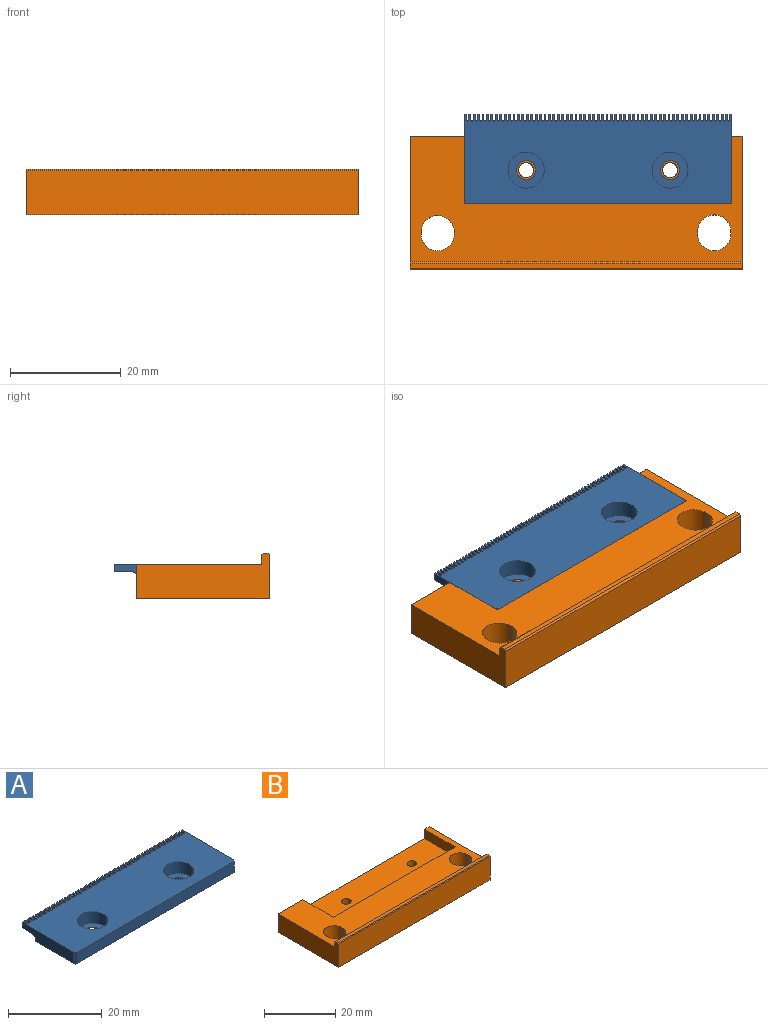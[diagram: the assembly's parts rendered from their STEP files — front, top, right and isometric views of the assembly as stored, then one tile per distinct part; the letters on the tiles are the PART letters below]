
ASSEMBLY  parts=2 mates=1
PART A: 260 faces, bbox 48.3x16.1x3.2 mm
  f0: plane 1.4x0.34mm, normal (0,1,0), area 0.5mm2, adj f67,f70,f71,f257
  f1: plane 1.4x0.34mm, normal (0,1,0), area 0.5mm2, adj f67,f73,f74,f257
  f2: plane 1.4x0.34mm, normal (0,1,0), area 0.5mm2, adj f67,f76,f77,f257
  f3: plane 1.4x0.34mm, normal (0,1,0), area 0.5mm2, adj f67,f79,f80,f257
  f4: plane 1.4x0.34mm, normal (0,1,0), area 0.5mm2, adj f67,f82,f83,f257
  f5: plane 1.4x0.34mm, normal (0,1,0), area 0.5mm2, adj f67,f85,f86,f257
  f6: plane 1.4x0.34mm, normal (0,1,0), area 0.5mm2, adj f67,f88,f89,f257
  f7: plane 1.4x0.34mm, normal (0,1,0), area 0.5mm2, adj f67,f91,f92,f257
  f8: plane 1.4x0.34mm, normal (0,1,0), area 0.5mm2, adj f67,f94,f95,f257
  f9: plane 1.4x0.34mm, normal (0,1,0), area 0.5mm2, adj f67,f97,f98,f257
  f10: plane 1.4x0.34mm, normal (0,1,0), area 0.5mm2, adj f67,f100,f101,f257
  f11: plane 1.4x0.34mm, normal (0,1,0), area 0.5mm2, adj f67,f103,f104,f257
  f12: plane 1.4x0.34mm, normal (0,1,0), area 0.5mm2, adj f67,f106,f107,f257
  f13: plane 1.4x0.34mm, normal (0,1,0), area 0.5mm2, adj f67,f109,f110,f257
  f14: plane 1.4x0.34mm, normal (0,1,0), area 0.5mm2, adj f67,f112,f113,f257
  f15: plane 1.4x0.34mm, normal (0,1,0), area 0.5mm2, adj f67,f115,f116,f257
  f16: plane 1.4x0.34mm, normal (0,1,0), area 0.5mm2, adj f67,f118,f119,f257
  f17: plane 1.4x0.34mm, normal (0,1,0), area 0.5mm2, adj f67,f121,f122,f257
  f18: plane 1.4x0.34mm, normal (0,1,0), area 0.5mm2, adj f67,f124,f125,f257
  f19: plane 1.4x0.34mm, normal (0,1,0), area 0.5mm2, adj f67,f127,f128,f257
  f20: plane 1.4x0.34mm, normal (0,1,0), area 0.5mm2, adj f67,f130,f131,f257
  f21: plane 1.4x0.34mm, normal (0,1,0), area 0.5mm2, adj f67,f133,f134,f257
  f22: plane 1.4x0.34mm, normal (0,1,0), area 0.5mm2, adj f67,f136,f137,f257
  f23: plane 1.4x0.34mm, normal (0,1,0), area 0.5mm2, adj f67,f139,f140,f257
  f24: plane 1.4x0.34mm, normal (0,1,0), area 0.5mm2, adj f67,f142,f143,f257
  f25: plane 1.4x0.34mm, normal (0,1,0), area 0.5mm2, adj f67,f145,f146,f257
  f26: plane 1.4x0.34mm, normal (0,1,0), area 0.5mm2, adj f67,f148,f149,f257
  f27: plane 1.4x0.34mm, normal (0,1,0), area 0.5mm2, adj f67,f151,f152,f257
  f28: plane 1.4x0.34mm, normal (0,1,0), area 0.5mm2, adj f67,f154,f155,f257
  f29: plane 1.4x0.34mm, normal (0,1,0), area 0.5mm2, adj f67,f157,f158,f257
  f30: plane 1.4x0.34mm, normal (0,1,0), area 0.5mm2, adj f67,f160,f161,f257
  f31: plane 1.4x0.34mm, normal (0,1,0), area 0.5mm2, adj f67,f163,f164,f257
  f32: plane 1.4x0.34mm, normal (0,1,0), area 0.5mm2, adj f67,f166,f167,f257
  f33: plane 1.4x0.34mm, normal (0,1,0), area 0.5mm2, adj f67,f169,f170,f257
  f34: plane 1.4x0.34mm, normal (0,1,0), area 0.5mm2, adj f67,f172,f173,f257
  f35: plane 1.4x0.34mm, normal (0,1,0), area 0.5mm2, adj f67,f175,f176,f257
  f36: plane 1.4x0.34mm, normal (0,1,0), area 0.5mm2, adj f67,f178,f179,f257
  f37: plane 1.4x0.34mm, normal (0,1,0), area 0.5mm2, adj f67,f181,f182,f257
  f38: plane 1.4x0.34mm, normal (0,1,0), area 0.5mm2, adj f67,f184,f185,f257
  f39: plane 1.4x0.34mm, normal (0,1,0), area 0.5mm2, adj f67,f187,f188,f257
  f40: plane 1.4x0.34mm, normal (0,1,0), area 0.5mm2, adj f67,f190,f191,f257
  f41: plane 1.4x0.34mm, normal (0,1,0), area 0.5mm2, adj f67,f193,f194,f257
  f42: plane 1.4x0.34mm, normal (0,1,0), area 0.5mm2, adj f67,f196,f197,f257
  f43: plane 1.4x0.34mm, normal (0,1,0), area 0.5mm2, adj f67,f199,f200,f257
  f44: plane 1.4x0.34mm, normal (0,1,0), area 0.5mm2, adj f67,f202,f203,f257
  f45: plane 1.4x0.34mm, normal (0,1,0), area 0.5mm2, adj f67,f205,f206,f257
  f46: plane 1.4x0.34mm, normal (0,1,0), area 0.5mm2, adj f67,f208,f209,f257
  f47: plane 1.4x0.34mm, normal (0,1,0), area 0.5mm2, adj f67,f211,f212,f257
  f48: plane 1.4x0.34mm, normal (0,1,0), area 0.5mm2, adj f67,f214,f215,f257
  f49: plane 1.4x0.34mm, normal (0,1,0), area 0.5mm2, adj f67,f217,f218,f257
  f50: plane 1.4x0.34mm, normal (0,1,0), area 0.5mm2, adj f67,f220,f221,f257
  f51: plane 1.4x0.34mm, normal (0,1,0), area 0.5mm2, adj f67,f223,f224,f257
  f52: plane 1.4x0.34mm, normal (0,1,0), area 0.5mm2, adj f67,f226,f227,f257
  f53: plane 1.4x0.34mm, normal (0,1,0), area 0.5mm2, adj f67,f229,f230,f257
  f54: plane 1.4x0.34mm, normal (0,1,0), area 0.5mm2, adj f67,f232,f233,f257
  f55: plane 1.4x0.34mm, normal (0,1,0), area 0.5mm2, adj f67,f235,f236,f257
  f56: plane 1.4x0.34mm, normal (0,1,0), area 0.5mm2, adj f67,f238,f239,f257
  f57: plane 1.4x0.34mm, normal (0,1,0), area 0.5mm2, adj f67,f241,f242,f257
  f58: plane 1.4x0.34mm, normal (0,1,0), area 0.5mm2, adj f67,f244,f245,f257
  f59: plane 15.6x2.85mm, normal (-1,0,0), area 38.7mm2, adj f62,f64,f67,f254,f257,f258,f259
  f60: plane 47.74x11.7mm, normal (0,0,-1), area 540.4mm2, adj f63,f64,f248,f251,f256,f259
  f61: plane 1.4x0.34mm, normal (0,1,0), area 0.5mm2, adj f66,f67,f68,f257
  f62: plane 1.4x0.34mm, normal (0,1,0), area 0.5mm2, adj f59,f67,f247,f257
  f63: plane 11.75x0.3mm, normal (0.71,0,-0.71), area 4.9mm2, adj f60,f66,f255,f256,f259
  f64: plane 11.75x0.3mm, normal (-0.71,0,-0.71), area 4.9mm2, adj f59,f60,f254,f256,f259
  f65: plane 47.34x2.85mm, normal (0,-1,0), area 134.9mm2, adj f67,f254,f255,f256
  f66: plane 15.6x2.85mm, normal (1,0,0), area 38.7mm2, adj f61,f63,f67,f255,f257,f258,f259
  f67: plane 48.34x16.1mm, normal (0,0,1), area 679.1mm2, adj f0,f1,f2,f3,f4,f5,f6,f7
  f68: plane 1.4x1mm, normal (-1,0,0), area 1.4mm2, adj f61,f67,f69,f257
  f69: cylinder r=0.23mm len=1.4mm, axis (0,0,-1), area 1mm2, adj f67,f68,f70,f257
  f70: plane 1.4x1mm, normal (1,0,0), area 1.4mm2, adj f0,f67,f69,f257
  f71: plane 1.4x1mm, normal (-1,0,0), area 1.4mm2, adj f0,f67,f72,f257
  f72: cylinder r=0.23mm len=1.4mm, axis (0,0,-1), area 1mm2, adj f67,f71,f73,f257
  f73: plane 1.4x1mm, normal (1,0,0), area 1.4mm2, adj f1,f67,f72,f257
  f74: plane 1.4x1mm, normal (-1,0,0), area 1.4mm2, adj f1,f67,f75,f257
  f75: cylinder r=0.23mm len=1.4mm, axis (0,0,-1), area 1mm2, adj f67,f74,f76,f257
  f76: plane 1.4x1mm, normal (1,0,0), area 1.4mm2, adj f2,f67,f75,f257
  f77: plane 1.4x1mm, normal (-1,0,0), area 1.4mm2, adj f2,f67,f78,f257
  f78: cylinder r=0.23mm len=1.4mm, axis (0,0,-1), area 1mm2, adj f67,f77,f79,f257
  f79: plane 1.4x1mm, normal (1,0,0), area 1.4mm2, adj f3,f67,f78,f257
  f80: plane 1.4x1mm, normal (-1,0,0), area 1.4mm2, adj f3,f67,f81,f257
  f81: cylinder r=0.23mm len=1.4mm, axis (0,0,-1), area 1mm2, adj f67,f80,f82,f257
  f82: plane 1.4x1mm, normal (1,0,0), area 1.4mm2, adj f4,f67,f81,f257
  f83: plane 1.4x1mm, normal (-1,0,0), area 1.4mm2, adj f4,f67,f84,f257
  f84: cylinder r=0.23mm len=1.4mm, axis (0,0,-1), area 1mm2, adj f67,f83,f85,f257
  f85: plane 1.4x1mm, normal (1,0,0), area 1.4mm2, adj f5,f67,f84,f257
  f86: plane 1.4x1mm, normal (-1,0,0), area 1.4mm2, adj f5,f67,f87,f257
  f87: cylinder r=0.23mm len=1.4mm, axis (0,0,-1), area 1mm2, adj f67,f86,f88,f257
  f88: plane 1.4x1mm, normal (1,0,0), area 1.4mm2, adj f6,f67,f87,f257
  f89: plane 1.4x1mm, normal (-1,0,0), area 1.4mm2, adj f6,f67,f90,f257
  f90: cylinder r=0.23mm len=1.4mm, axis (0,0,-1), area 1mm2, adj f67,f89,f91,f257
  f91: plane 1.4x1mm, normal (1,0,0), area 1.4mm2, adj f7,f67,f90,f257
  f92: plane 1.4x1mm, normal (-1,0,0), area 1.4mm2, adj f7,f67,f93,f257
  f93: cylinder r=0.23mm len=1.4mm, axis (0,0,-1), area 1mm2, adj f67,f92,f94,f257
  f94: plane 1.4x1mm, normal (1,0,0), area 1.4mm2, adj f8,f67,f93,f257
  f95: plane 1.4x1mm, normal (-1,0,0), area 1.4mm2, adj f8,f67,f96,f257
  f96: cylinder r=0.23mm len=1.4mm, axis (0,0,-1), area 1mm2, adj f67,f95,f97,f257
  f97: plane 1.4x1mm, normal (1,0,0), area 1.4mm2, adj f9,f67,f96,f257
  f98: plane 1.4x1mm, normal (-1,0,0), area 1.4mm2, adj f9,f67,f99,f257
  f99: cylinder r=0.23mm len=1.4mm, axis (0,0,-1), area 1mm2, adj f67,f98,f100,f257
  f100: plane 1.4x1mm, normal (1,0,0), area 1.4mm2, adj f10,f67,f99,f257
  f101: plane 1.4x1mm, normal (-1,0,0), area 1.4mm2, adj f10,f67,f102,f257
  f102: cylinder r=0.23mm len=1.4mm, axis (0,0,-1), area 1mm2, adj f67,f101,f103,f257
  f103: plane 1.4x1mm, normal (1,0,0), area 1.4mm2, adj f11,f67,f102,f257
  f104: plane 1.4x1mm, normal (-1,0,0), area 1.4mm2, adj f11,f67,f105,f257
  f105: cylinder r=0.23mm len=1.4mm, axis (0,0,-1), area 1mm2, adj f67,f104,f106,f257
  f106: plane 1.4x1mm, normal (1,0,0), area 1.4mm2, adj f12,f67,f105,f257
  f107: plane 1.4x1mm, normal (-1,0,0), area 1.4mm2, adj f12,f67,f108,f257
  f108: cylinder r=0.23mm len=1.4mm, axis (0,0,-1), area 1mm2, adj f67,f107,f109,f257
  f109: plane 1.4x1mm, normal (1,0,0), area 1.4mm2, adj f13,f67,f108,f257
  f110: plane 1.4x1mm, normal (-1,0,0), area 1.4mm2, adj f13,f67,f111,f257
  f111: cylinder r=0.23mm len=1.4mm, axis (0,0,-1), area 1mm2, adj f67,f110,f112,f257
  f112: plane 1.4x1mm, normal (1,0,0), area 1.4mm2, adj f14,f67,f111,f257
  f113: plane 1.4x1mm, normal (-1,0,0), area 1.4mm2, adj f14,f67,f114,f257
  f114: cylinder r=0.23mm len=1.4mm, axis (0,0,-1), area 1mm2, adj f67,f113,f115,f257
  f115: plane 1.4x1mm, normal (1,0,0), area 1.4mm2, adj f15,f67,f114,f257
  f116: plane 1.4x1mm, normal (-1,0,0), area 1.4mm2, adj f15,f67,f117,f257
  f117: cylinder r=0.23mm len=1.4mm, axis (0,0,-1), area 1mm2, adj f67,f116,f118,f257
  f118: plane 1.4x1mm, normal (1,0,0), area 1.4mm2, adj f16,f67,f117,f257
  f119: plane 1.4x1mm, normal (-1,0,0), area 1.4mm2, adj f16,f67,f120,f257
  f120: cylinder r=0.23mm len=1.4mm, axis (0,0,-1), area 1mm2, adj f67,f119,f121,f257
  f121: plane 1.4x1mm, normal (1,0,0), area 1.4mm2, adj f17,f67,f120,f257
  f122: plane 1.4x1mm, normal (-1,0,0), area 1.4mm2, adj f17,f67,f123,f257
  f123: cylinder r=0.23mm len=1.4mm, axis (0,0,-1), area 1mm2, adj f67,f122,f124,f257
  f124: plane 1.4x1mm, normal (1,0,0), area 1.4mm2, adj f18,f67,f123,f257
  f125: plane 1.4x1mm, normal (-1,0,0), area 1.4mm2, adj f18,f67,f126,f257
  f126: cylinder r=0.23mm len=1.4mm, axis (0,0,-1), area 1mm2, adj f67,f125,f127,f257
  f127: plane 1.4x1mm, normal (1,0,0), area 1.4mm2, adj f19,f67,f126,f257
  f128: plane 1.4x1mm, normal (-1,0,0), area 1.4mm2, adj f19,f67,f129,f257
  f129: cylinder r=0.23mm len=1.4mm, axis (0,0,-1), area 1mm2, adj f67,f128,f130,f257
  f130: plane 1.4x1mm, normal (1,0,0), area 1.4mm2, adj f20,f67,f129,f257
  f131: plane 1.4x1mm, normal (-1,0,0), area 1.4mm2, adj f20,f67,f132,f257
  f132: cylinder r=0.23mm len=1.4mm, axis (0,0,-1), area 1mm2, adj f67,f131,f133,f257
  f133: plane 1.4x1mm, normal (1,0,0), area 1.4mm2, adj f21,f67,f132,f257
  f134: plane 1.4x1mm, normal (-1,0,0), area 1.4mm2, adj f21,f67,f135,f257
  f135: cylinder r=0.23mm len=1.4mm, axis (0,0,-1), area 1mm2, adj f67,f134,f136,f257
  f136: plane 1.4x1mm, normal (1,0,0), area 1.4mm2, adj f22,f67,f135,f257
  f137: plane 1.4x1mm, normal (-1,0,0), area 1.4mm2, adj f22,f67,f138,f257
  f138: cylinder r=0.23mm len=1.4mm, axis (0,0,-1), area 1mm2, adj f67,f137,f139,f257
  f139: plane 1.4x1mm, normal (1,0,0), area 1.4mm2, adj f23,f67,f138,f257
  f140: plane 1.4x1mm, normal (-1,0,0), area 1.4mm2, adj f23,f67,f141,f257
  f141: cylinder r=0.23mm len=1.4mm, axis (0,0,-1), area 1mm2, adj f67,f140,f142,f257
  f142: plane 1.4x1mm, normal (1,0,0), area 1.4mm2, adj f24,f67,f141,f257
  f143: plane 1.4x1mm, normal (-1,0,0), area 1.4mm2, adj f24,f67,f144,f257
  f144: cylinder r=0.23mm len=1.4mm, axis (0,0,-1), area 1mm2, adj f67,f143,f145,f257
  f145: plane 1.4x1mm, normal (1,0,0), area 1.4mm2, adj f25,f67,f144,f257
  f146: plane 1.4x1mm, normal (-1,0,0), area 1.4mm2, adj f25,f67,f147,f257
  f147: cylinder r=0.23mm len=1.4mm, axis (0,0,-1), area 1mm2, adj f67,f146,f148,f257
  f148: plane 1.4x1mm, normal (1,0,0), area 1.4mm2, adj f26,f67,f147,f257
  f149: plane 1.4x1mm, normal (-1,0,0), area 1.4mm2, adj f26,f67,f150,f257
  f150: cylinder r=0.23mm len=1.4mm, axis (0,0,-1), area 1mm2, adj f67,f149,f151,f257
  f151: plane 1.4x1mm, normal (1,0,0), area 1.4mm2, adj f27,f67,f150,f257
  f152: plane 1.4x1mm, normal (-1,0,0), area 1.4mm2, adj f27,f67,f153,f257
  f153: cylinder r=0.23mm len=1.4mm, axis (0,0,-1), area 1mm2, adj f67,f152,f154,f257
  f154: plane 1.4x1mm, normal (1,0,0), area 1.4mm2, adj f28,f67,f153,f257
  f155: plane 1.4x1mm, normal (-1,0,0), area 1.4mm2, adj f28,f67,f156,f257
  f156: cylinder r=0.23mm len=1.4mm, axis (0,0,-1), area 1mm2, adj f67,f155,f157,f257
  f157: plane 1.4x1mm, normal (1,0,0), area 1.4mm2, adj f29,f67,f156,f257
  f158: plane 1.4x1mm, normal (-1,0,0), area 1.4mm2, adj f29,f67,f159,f257
  f159: cylinder r=0.23mm len=1.4mm, axis (0,0,-1), area 1mm2, adj f67,f158,f160,f257
  f160: plane 1.4x1mm, normal (1,0,0), area 1.4mm2, adj f30,f67,f159,f257
  f161: plane 1.4x1mm, normal (-1,0,0), area 1.4mm2, adj f30,f67,f162,f257
  f162: cylinder r=0.23mm len=1.4mm, axis (0,0,-1), area 1mm2, adj f67,f161,f163,f257
  f163: plane 1.4x1mm, normal (1,0,0), area 1.4mm2, adj f31,f67,f162,f257
  f164: plane 1.4x1mm, normal (-1,0,0), area 1.4mm2, adj f31,f67,f165,f257
  f165: cylinder r=0.23mm len=1.4mm, axis (0,0,-1), area 1mm2, adj f67,f164,f166,f257
  f166: plane 1.4x1mm, normal (1,0,0), area 1.4mm2, adj f32,f67,f165,f257
  f167: plane 1.4x1mm, normal (-1,0,0), area 1.4mm2, adj f32,f67,f168,f257
  f168: cylinder r=0.23mm len=1.4mm, axis (0,0,-1), area 1mm2, adj f67,f167,f169,f257
  f169: plane 1.4x1mm, normal (1,0,0), area 1.4mm2, adj f33,f67,f168,f257
  f170: plane 1.4x1mm, normal (-1,0,0), area 1.4mm2, adj f33,f67,f171,f257
  f171: cylinder r=0.23mm len=1.4mm, axis (0,0,-1), area 1mm2, adj f67,f170,f172,f257
  f172: plane 1.4x1mm, normal (1,0,0), area 1.4mm2, adj f34,f67,f171,f257
  f173: plane 1.4x1mm, normal (-1,0,0), area 1.4mm2, adj f34,f67,f174,f257
  f174: cylinder r=0.23mm len=1.4mm, axis (0,0,-1), area 1mm2, adj f67,f173,f175,f257
  f175: plane 1.4x1mm, normal (1,0,0), area 1.4mm2, adj f35,f67,f174,f257
  f176: plane 1.4x1mm, normal (-1,0,0), area 1.4mm2, adj f35,f67,f177,f257
  f177: cylinder r=0.23mm len=1.4mm, axis (0,0,-1), area 1mm2, adj f67,f176,f178,f257
  f178: plane 1.4x1mm, normal (1,0,0), area 1.4mm2, adj f36,f67,f177,f257
  f179: plane 1.4x1mm, normal (-1,0,0), area 1.4mm2, adj f36,f67,f180,f257
  f180: cylinder r=0.23mm len=1.4mm, axis (0,0,-1), area 1mm2, adj f67,f179,f181,f257
  f181: plane 1.4x1mm, normal (1,0,0), area 1.4mm2, adj f37,f67,f180,f257
  f182: plane 1.4x1mm, normal (-1,0,0), area 1.4mm2, adj f37,f67,f183,f257
  f183: cylinder r=0.23mm len=1.4mm, axis (0,0,-1), area 1mm2, adj f67,f182,f184,f257
  f184: plane 1.4x1mm, normal (1,0,0), area 1.4mm2, adj f38,f67,f183,f257
  f185: plane 1.4x1mm, normal (-1,0,0), area 1.4mm2, adj f38,f67,f186,f257
  f186: cylinder r=0.23mm len=1.4mm, axis (0,0,-1), area 1mm2, adj f67,f185,f187,f257
  f187: plane 1.4x1mm, normal (1,0,0), area 1.4mm2, adj f39,f67,f186,f257
  f188: plane 1.4x1mm, normal (-1,0,0), area 1.4mm2, adj f39,f67,f189,f257
  f189: cylinder r=0.23mm len=1.4mm, axis (0,0,-1), area 1mm2, adj f67,f188,f190,f257
  f190: plane 1.4x1mm, normal (1,0,0), area 1.4mm2, adj f40,f67,f189,f257
  f191: plane 1.4x1mm, normal (-1,0,0), area 1.4mm2, adj f40,f67,f192,f257
  f192: cylinder r=0.23mm len=1.4mm, axis (0,0,-1), area 1mm2, adj f67,f191,f193,f257
  f193: plane 1.4x1mm, normal (1,0,0), area 1.4mm2, adj f41,f67,f192,f257
  f194: plane 1.4x1mm, normal (-1,0,0), area 1.4mm2, adj f41,f67,f195,f257
  f195: cylinder r=0.23mm len=1.4mm, axis (0,0,-1), area 1mm2, adj f67,f194,f196,f257
  f196: plane 1.4x1mm, normal (1,0,0), area 1.4mm2, adj f42,f67,f195,f257
  f197: plane 1.4x1mm, normal (-1,0,0), area 1.4mm2, adj f42,f67,f198,f257
  f198: cylinder r=0.23mm len=1.4mm, axis (0,0,-1), area 1mm2, adj f67,f197,f199,f257
  f199: plane 1.4x1mm, normal (1,0,0), area 1.4mm2, adj f43,f67,f198,f257
  f200: plane 1.4x1mm, normal (-1,0,0), area 1.4mm2, adj f43,f67,f201,f257
  f201: cylinder r=0.23mm len=1.4mm, axis (0,0,-1), area 1mm2, adj f67,f200,f202,f257
  f202: plane 1.4x1mm, normal (1,0,0), area 1.4mm2, adj f44,f67,f201,f257
  f203: plane 1.4x1mm, normal (-1,0,0), area 1.4mm2, adj f44,f67,f204,f257
  f204: cylinder r=0.23mm len=1.4mm, axis (0,0,-1), area 1mm2, adj f67,f203,f205,f257
  f205: plane 1.4x1mm, normal (1,0,0), area 1.4mm2, adj f45,f67,f204,f257
  f206: plane 1.4x1mm, normal (-1,0,0), area 1.4mm2, adj f45,f67,f207,f257
  f207: cylinder r=0.23mm len=1.4mm, axis (0,0,-1), area 1mm2, adj f67,f206,f208,f257
  f208: plane 1.4x1mm, normal (1,0,0), area 1.4mm2, adj f46,f67,f207,f257
  f209: plane 1.4x1mm, normal (-1,0,0), area 1.4mm2, adj f46,f67,f210,f257
  f210: cylinder r=0.23mm len=1.4mm, axis (0,0,-1), area 1mm2, adj f67,f209,f211,f257
  f211: plane 1.4x1mm, normal (1,0,0), area 1.4mm2, adj f47,f67,f210,f257
  f212: plane 1.4x1mm, normal (-1,0,0), area 1.4mm2, adj f47,f67,f213,f257
  f213: cylinder r=0.23mm len=1.4mm, axis (0,0,-1), area 1mm2, adj f67,f212,f214,f257
  f214: plane 1.4x1mm, normal (1,0,0), area 1.4mm2, adj f48,f67,f213,f257
  f215: plane 1.4x1mm, normal (-1,0,0), area 1.4mm2, adj f48,f67,f216,f257
  f216: cylinder r=0.23mm len=1.4mm, axis (0,0,-1), area 1mm2, adj f67,f215,f217,f257
  f217: plane 1.4x1mm, normal (1,0,0), area 1.4mm2, adj f49,f67,f216,f257
  f218: plane 1.4x1mm, normal (-1,0,0), area 1.4mm2, adj f49,f67,f219,f257
  f219: cylinder r=0.23mm len=1.4mm, axis (0,0,-1), area 1mm2, adj f67,f218,f220,f257
  f220: plane 1.4x1mm, normal (1,0,0), area 1.4mm2, adj f50,f67,f219,f257
  f221: plane 1.4x1mm, normal (-1,0,0), area 1.4mm2, adj f50,f67,f222,f257
  f222: cylinder r=0.23mm len=1.4mm, axis (0,0,-1), area 1mm2, adj f67,f221,f223,f257
  f223: plane 1.4x1mm, normal (1,0,0), area 1.4mm2, adj f51,f67,f222,f257
  f224: plane 1.4x1mm, normal (-1,0,0), area 1.4mm2, adj f51,f67,f225,f257
  f225: cylinder r=0.23mm len=1.4mm, axis (0,0,-1), area 1mm2, adj f67,f224,f226,f257
  f226: plane 1.4x1mm, normal (1,0,0), area 1.4mm2, adj f52,f67,f225,f257
  f227: plane 1.4x1mm, normal (-1,0,0), area 1.4mm2, adj f52,f67,f228,f257
  f228: cylinder r=0.23mm len=1.4mm, axis (0,0,-1), area 1mm2, adj f67,f227,f229,f257
  f229: plane 1.4x1mm, normal (1,0,0), area 1.4mm2, adj f53,f67,f228,f257
  f230: plane 1.4x1mm, normal (-1,0,0), area 1.4mm2, adj f53,f67,f231,f257
  f231: cylinder r=0.23mm len=1.4mm, axis (0,0,-1), area 1mm2, adj f67,f230,f232,f257
  f232: plane 1.4x1mm, normal (1,0,0), area 1.4mm2, adj f54,f67,f231,f257
  f233: plane 1.4x1mm, normal (-1,0,0), area 1.4mm2, adj f54,f67,f234,f257
  f234: cylinder r=0.23mm len=1.4mm, axis (0,0,-1), area 1mm2, adj f67,f233,f235,f257
  f235: plane 1.4x1mm, normal (1,0,0), area 1.4mm2, adj f55,f67,f234,f257
  f236: plane 1.4x1mm, normal (-1,0,0), area 1.4mm2, adj f55,f67,f237,f257
  f237: cylinder r=0.23mm len=1.4mm, axis (0,0,-1), area 1mm2, adj f67,f236,f238,f257
  f238: plane 1.4x1mm, normal (1,0,0), area 1.4mm2, adj f56,f67,f237,f257
  f239: plane 1.4x1mm, normal (-1,0,0), area 1.4mm2, adj f56,f67,f240,f257
  f240: cylinder r=0.23mm len=1.4mm, axis (0,0,-1), area 1mm2, adj f67,f239,f241,f257
  f241: plane 1.4x1mm, normal (1,0,0), area 1.4mm2, adj f57,f67,f240,f257
  f242: plane 1.4x1mm, normal (-1,0,0), area 1.4mm2, adj f57,f67,f243,f257
  f243: cylinder r=0.23mm len=1.4mm, axis (0,0,-1), area 1mm2, adj f67,f242,f244,f257
  f244: plane 1.4x1mm, normal (1,0,0), area 1.4mm2, adj f58,f67,f243,f257
  f245: plane 1.4x1mm, normal (-1,0,0), area 1.4mm2, adj f58,f67,f246,f257
  f246: cylinder r=0.23mm len=1.4mm, axis (0,0,-1), area 1mm2, adj f67,f245,f247,f257
  f247: plane 1.4x1mm, normal (1,0,0), area 1.4mm2, adj f62,f67,f246,f257
  f248: cylinder r=1.7mm len=3.4mm, axis (0,0,1), area 1.6mm2, adj f60,f249
  f249: plane 6.5x6.5mm, normal (0,0,1), area 24.1mm2, adj f248,f250
  f250: cylinder r=3.25mm len=6.5mm, axis (0,0,1), area 61.3mm2, adj f67,f249
  f251: cylinder r=1.7mm len=3.4mm, axis (0,0,1), area 1.6mm2, adj f60,f252
  f252: plane 6.5x6.5mm, normal (0,0,1), area 24.1mm2, adj f251,f253
  f253: cylinder r=3.25mm len=6.5mm, axis (0,0,1), area 61.3mm2, adj f67,f252
  f254: plane 3.1x0.5mm, normal (-0.71,-0.71,0), area 2.1mm2, adj f59,f64,f65,f67,f256
  f255: plane 3.1x0.5mm, normal (0.71,-0.71,0), area 2.1mm2, adj f63,f65,f66,f67,f256
  f256: plane 47.84x0.3mm, normal (0,-0.71,-0.71), area 20.2mm2, adj f60,f63,f64,f65,f254,f255
  f257: plane 48.34x3.2mm, normal (0,0,-1), area 122.1mm2, adj f0,f1,f2,f3,f4,f5,f6,f7
  f258: cylinder r=0.9mm len=48.34mm, axis (1,0,0), area 68.3mm2, adj f59,f66,f257,f259
  f259: plane 48.34x0.85mm, normal (0,1,0), area 41mm2, adj f59,f60,f63,f64,f66,f258
PART B: 24 faces, bbox 60x24.1x8.3 mm
  f0: plane 60x22.6mm, normal (0,0,1), area 709.3mm2, adj f2,f3,f4,f5,f7,f8,f9,f13
  f1: plane 60x24.1mm, normal (0,0,-1), area 1372.8mm2, adj f5,f6,f7,f8,f13,f14,f15,f16
  f2: plane 12.1x3.15mm, normal (-1,0,0), area 38.1mm2, adj f0,f3,f8,f21
  f3: plane 48.34x3.15mm, normal (0,1,0), area 152.3mm2, adj f0,f2,f4,f21
  f4: plane 12.1x3.15mm, normal (1,0,0), area 38.1mm2, adj f0,f3,f8,f21
  f5: plane 24.1x8.3mm, normal (-1,0,0), area 154.7mm2, adj f0,f1,f6,f8,f9,f10,f11,f12
  f6: plane 60x8mm, normal (0,-1,0), area 480mm2, adj f1,f5,f7,f12
  f7: plane 24.1x8.3mm, normal (1,0,0), area 154.7mm2, adj f0,f1,f6,f8,f9,f10,f11,f12
  f8: plane 60x6.3mm, normal (0,1,0), area 225.7mm2, adj f0,f1,f2,f4,f5,f7,f21
  f9: plane 60x1.7mm, normal (0,1,0), area 102mm2, adj f0,f5,f7,f11
  f10: plane 60x0.9mm, normal (0,0,1), area 54mm2, adj f5,f7,f11,f12
  f11: plane 60x0.3mm, normal (0,0.71,0.71), area 25.5mm2, adj f5,f7,f9,f10
  f12: plane 60x0.3mm, normal (0,-0.71,0.71), area 25.5mm2, adj f5,f6,f7,f10
  f13: plane 6.3x0.5mm, normal (-1,0,0), area 3.1mm2, adj f0,f1,f14,f16
  f14: cylinder r=3mm len=6.3mm, axis (0,0,1), area 59.4mm2, adj f0,f1,f13,f15
  f15: plane 6.3x0.5mm, normal (1,0,0), area 3.1mm2, adj f0,f1,f14,f16
  f16: cylinder r=3mm len=6.3mm, axis (0,0,1), area 59.4mm2, adj f0,f1,f13,f15
  f17: plane 6.3x0.5mm, normal (-1,0,0), area 3.2mm2, adj f0,f1,f18,f20
  f18: cylinder r=3mm len=6.3mm, axis (0,0,1), area 59.7mm2, adj f0,f1,f17,f19
  f19: plane 6.3x0.13mm, normal (-0.99,0.11,0), area 0.8mm2, adj f0,f1,f18,f20
  f20: cylinder r=3mm len=6.3mm, axis (0,0,1), area 61.4mm2, adj f0,f1,f17,f19
  f21: plane 48.34x12.1mm, normal (0,0,1), area 573.5mm2, adj f2,f3,f4,f8,f22,f23
  f22: cylinder r=1.35mm len=3.15mm, axis (0,0,-1), area 26.7mm2, adj f1,f21
  f23: cylinder r=1.35mm len=3.15mm, axis (0,0,-1), area 26.7mm2, adj f1,f21
PLACE A t=(3.24,23.22,-5.07)mm
PLACE B t=(-6.59,11.22,-8.22)mm
MATE fastened A.f251 <-> B.f23  axis (0,0,-1) through (14.41,29.22,-5.07)mm
